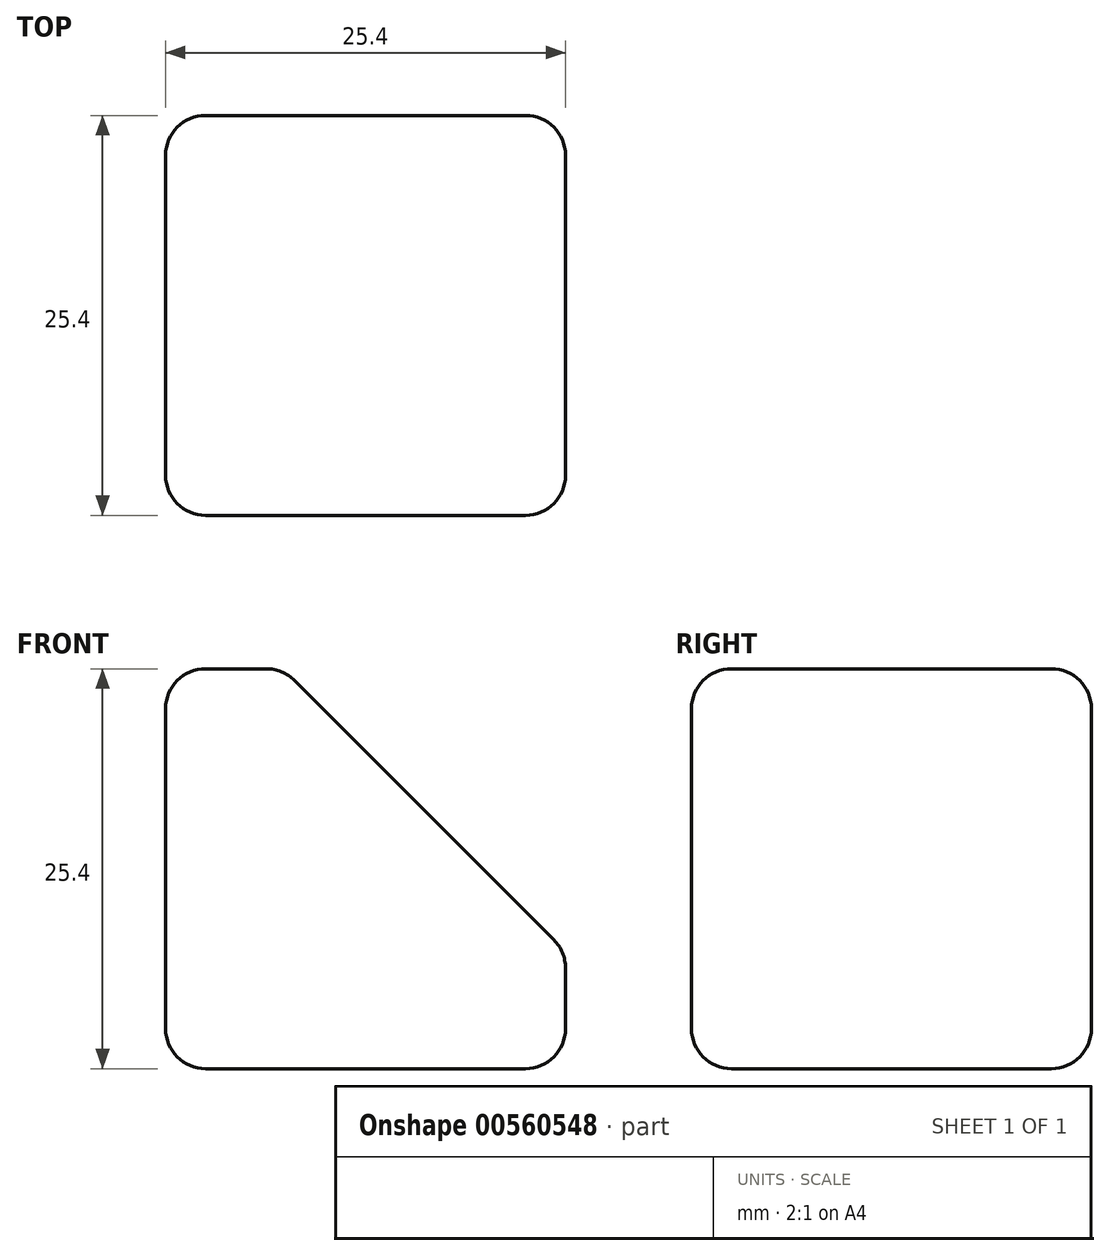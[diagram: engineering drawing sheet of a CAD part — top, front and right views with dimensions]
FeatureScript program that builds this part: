
annotation { "Feature Type Name" : "Feature", "Feature Type Description" : "" }
export const myFeature = defineFeature(function(context is Context, id is Id, definition is map)
    precondition{}
    {
        {
            var Q0;
            Q0=qCreatedBy(makeId("Front.planeOp"),FACE);
            var sketch = newSketch(context, id + "F0", { "sketchPlane" : qUnion([Q0])});
            skLineSegment(sketch, "E0.bottom", {"start": v(-12.7, -12.7) * mm, "end": v(12.7, -12.7) * mm});
            skLineSegment(sketch, "E0.top", {"start": v(-12.7, 12.7) * mm, "end": v(-5.26, 12.7) * mm});
            skLineSegment(sketch, "E0.left", {"start": v(-12.7, -12.7) * mm, "end": v(-12.7, 12.7) * mm});
            skLineSegment(sketch, "E0.right", {"start": v(12.7, -12.7) * mm, "end": v(12.7, -5.26) * mm});
            skPoint(sketch, "E0.middle", {"position": v(0, 0) * mm});
            skLineSegment(sketch, "E1", {"start": v(-5.26, 12.7) * mm, "end": v(12.7, -5.26) * mm});
            skPoint(sketch, "E2.orphan", {"position": v(12.7, 12.7) * mm});
            skSolve(sketch);
        }
        {
            var Q0;
            Q0 = qSketchRegion(id + "F0", true);
            extrude(context, id + "F1", {"entities" : qUnion([Q0]), "depth" : 25.4 * mm, "offsetDistance" : 25.4 * mm});
        }
        {
            var Q0;
            Q0=makeQuery(id+"F1.opExtrude","SWEPT_EDGE",EDGE,{"disambiguationData":[OSD([sQuery(id+"F0.wireOp",EDGE,"E0.top"),sQuery(id+"F0.wireOp",EDGE,"E0.left")])]});
            var Q1;
            Q1=makeQuery(id+"F1.opExtrude","SWEPT_FACE",FACE,{"disambiguationData":[OSD([sQuery(id+"F0.wireOp",EDGE,"E1")])]});
            var Q2;
            Q2=makeQuery(id+"F1.opExtrude","CAP_FACE",FACE,{"disambiguationData":[OSD([sQuery(id+"F0.wireOp",EDGE,"E0.bottom"),sQuery(id+"F0.wireOp",EDGE,"E0.top"),sQuery(id+"F0.wireOp",EDGE,"E0.left"),sQuery(id+"F0.wireOp",EDGE,"E0.right"),sQuery(id+"F0.wireOp",EDGE,"E1")])],"isStart":false});
            var Q3;
            Q3=makeQuery(id+"F1.opExtrude","SWEPT_FACE",FACE,{"disambiguationData":[OSD([sQuery(id+"F0.wireOp",EDGE,"E0.right")])]});
            var Q4;
            Q4=makeQuery(id+"F1.opExtrude","CAP_FACE",FACE,{"disambiguationData":[OSD([sQuery(id+"F0.wireOp",EDGE,"E0.bottom"),sQuery(id+"F0.wireOp",EDGE,"E0.top"),sQuery(id+"F0.wireOp",EDGE,"E0.left"),sQuery(id+"F0.wireOp",EDGE,"E0.right"),sQuery(id+"F0.wireOp",EDGE,"E1")])],"isStart":true});
            var Q5;
            Q5=makeQuery(id+"F1.opExtrude","SWEPT_EDGE",EDGE,{"disambiguationData":[OSD([sQuery(id+"F0.wireOp",EDGE,"E0.bottom"),sQuery(id+"F0.wireOp",EDGE,"E0.left")])]});
            fillet(context, id + "F2", {"entities" : qUnion([Q0, Q1, Q2, Q3, Q4, Q5]), "radius" : 2.54 * mm, "tangentPropagation" : true, "allowEdgeOverflow" : false});
        }
    });
